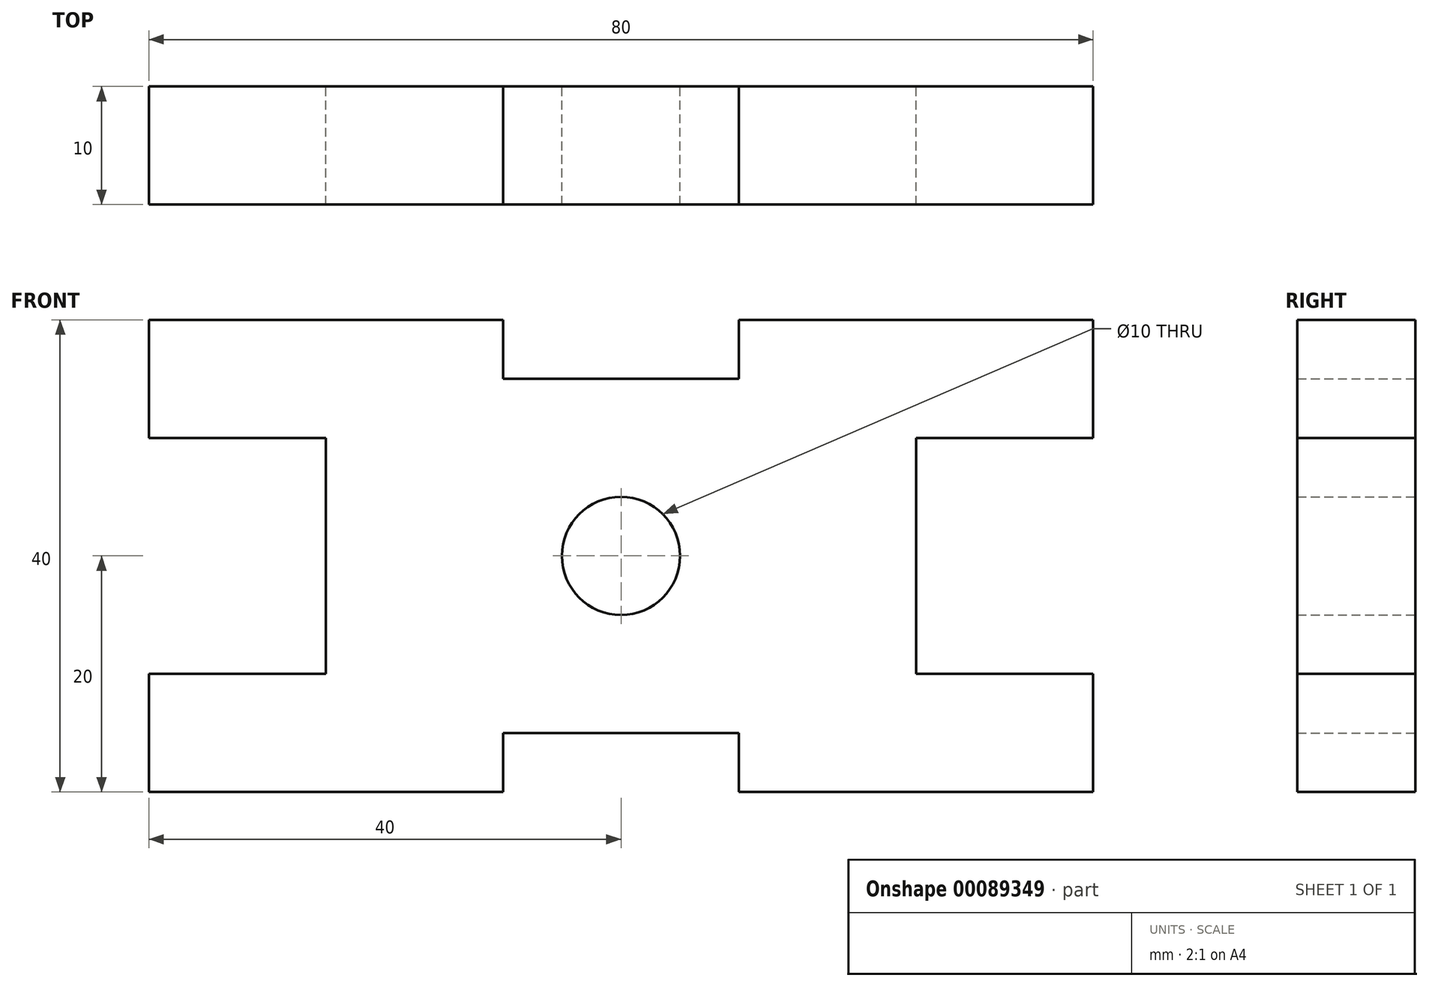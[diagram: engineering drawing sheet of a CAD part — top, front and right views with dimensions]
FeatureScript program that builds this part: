
annotation { "Feature Type Name" : "Feature", "Feature Type Description" : "" }
export const myFeature = defineFeature(function(context is Context, id is Id, definition is map)
    precondition{}
    {
        {
            var Q0;
            Q0=qCreatedBy(makeId("Front.planeOp"),FACE);
            var sketch = newSketch(context, id + "F0", { "sketchPlane" : qUnion([Q0])});
            skLineSegment(sketch, "E0", {"start": v(25, 10) * mm, "end": v(25, -10) * mm});
            skLineSegment(sketch, "E1", {"start": v(25, 10) * mm, "end": v(40, 10) * mm});
            skLineSegment(sketch, "E2", {"start": v(40, 10) * mm, "end": v(40, 20) * mm});
            skLineSegment(sketch, "E3", {"start": v(25, -10) * mm, "end": v(40, -10) * mm});
            skLineSegment(sketch, "E4", {"start": v(40, -10) * mm, "end": v(40, -20) * mm});
            skLineSegment(sketch, "E5", {"start": v(40, 20) * mm, "end": v(10, 20) * mm});
            skLineSegment(sketch, "E6", {"start": v(10, 20) * mm, "end": v(10, 15) * mm});
            skLineSegment(sketch, "E7", {"start": v(10, 15) * mm, "end": v(-10, 15) * mm});
            skLineSegment(sketch, "E8", {"start": v(-10, 15) * mm, "end": v(-10, 20) * mm});
            skLineSegment(sketch, "E9", {"start": v(-10, 20) * mm, "end": v(-40, 20) * mm});
            skLineSegment(sketch, "E10", {"start": v(-40, 20) * mm, "end": v(-40, 10) * mm});
            skLineSegment(sketch, "E11", {"start": v(-40, 10) * mm, "end": v(-25, 10) * mm});
            skLineSegment(sketch, "E12", {"start": v(-25, 10) * mm, "end": v(-25, -10) * mm});
            skLineSegment(sketch, "E13", {"start": v(-25, -10) * mm, "end": v(-40, -10) * mm});
            skLineSegment(sketch, "E14", {"start": v(-40, -10) * mm, "end": v(-40, -20) * mm});
            skLineSegment(sketch, "E15", {"start": v(-40, -20) * mm, "end": v(-10, -20) * mm});
            skLineSegment(sketch, "E16", {"start": v(-10, -20) * mm, "end": v(-10, -15) * mm});
            skLineSegment(sketch, "E17", {"start": v(-10, -15) * mm, "end": v(10, -15) * mm});
            skLineSegment(sketch, "E18", {"start": v(10, -15) * mm, "end": v(10, -20) * mm});
            skLineSegment(sketch, "E19", {"start": v(10, -20) * mm, "end": v(40, -20) * mm});
            skLineSegment(sketch, "E20", {"start": v(0, 15) * mm, "end": v(0, -15) * mm, "construction": true});
            skLineSegment(sketch, "E21", {"start": v(-25, 0) * mm, "end": v(25, 0) * mm, "construction": true});
            skCircle(sketch, "E22", {"center": v(0, 0) * mm, "radius": 5 * mm});
            skSolve(sketch);
        }
        {
            var Q0;
            Q0 = qSketchRegion(id + "F0", true);
            extrude(context, id + "F1", {"entities" : qUnion([Q0]), "depth" : 10 * mm});
        }
    });
